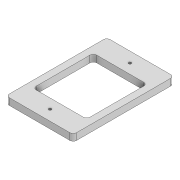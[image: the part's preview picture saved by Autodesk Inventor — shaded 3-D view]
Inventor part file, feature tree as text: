
AUTODESK INVENTOR PART (.ipt)
format: ipt  version: 2020 (Build 240168000, 168)  size: 113,664 bytes
history: native  units: mm
features: extrude x2, fillet x2, sketch x2
ambient origin geometry x8: Origin, YZ Plane, XZ Plane, XY Plane, X Axis, Y Axis, Z Axis, Center Point
bodies: Solid1 (feature_tree)
feature tree (6):
  extrude  "Extrusion1"  Depth=100.0mm
  fillet  "Fillet1"  Radius=59.5mm
  extrude  "Extrusion2"  Depth=10.0mm TaperAngle=0.0deg
  fillet  "Fillet2"  Radius=5.0mm
  sketch  "Sketch1"  dims[d0=150.0mm d1=100.0mm d2=59.5mm]
  sketch  "Sketch2"  dims[d3=4.0mm d4=10.0mm d5=0.0mm d6=5.0mm d7=90.0mm d8=80.0mm d9=10.0mm d10=0.0mm d11=5.0mm]
